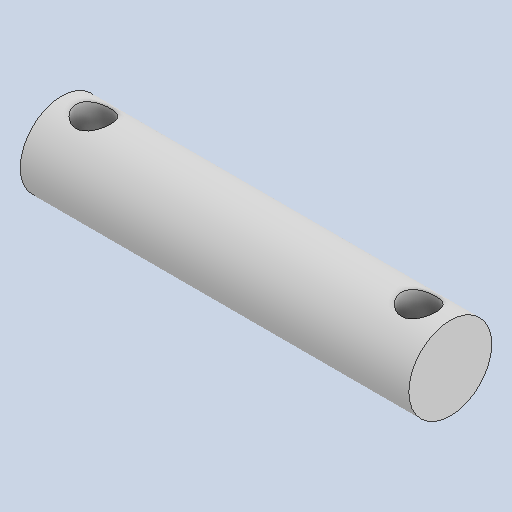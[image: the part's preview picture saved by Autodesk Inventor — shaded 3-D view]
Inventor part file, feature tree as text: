
AUTODESK INVENTOR PART (.ipt)
format: ipt  version: 2023 (Build 270158000, 158)  size: 243,712 bytes
history: native  units: in
note: dims shown in document units (in); Inventor stores cm internally (conversion verified against a paired STEP export)
features: extrude x2, sketch x2, plane x1
ambient origin geometry x8: Origin, YZ Plane, XZ Plane, XY Plane, X Axis, Y Axis, Z Axis, Center Point
bodies: Solid1 (feature_tree)
feature tree (5):
  extrude  "Extrusion1"  Depth=1.125in TaperAngle=0.0deg
  plane  "Work Plane1"
  extrude  "Extrusion2"  Depth=0.471in
  sketch  "Sketch1"  dims[d0=0.24in d1=1.125in d2=0.0in]
  sketch  "Sketch2"  dims[d3=0.1875in d4=0.471in d5=0.471in d6=0.1in d7=1.0in d8=0.0in d9=0.1in]
